# Revit family: xTub_Filler-American_Standard-Fluent-7186_Series
name_source: partatom
category: Plumbing Fixtures
revit_build: Autodesk Revit 2014 (Build: 20130308_1515(x64)
units: mm (PartAtom-declared; Revit-internal decimal feet)

## types (2) — shared parameters
8888.900 Deck-Mount Tub Filler Flex Hose Kit = No
ADA Compliant = Yes
Assembly Code = D2020300
CW Connection = Yes
CWFU = 3
Cold Water Connection Diameter = 3/4"
Default Elevation = 0"
Finish = Metal-American Standard-002-Polished Chrome
Flow Rate = 2.5 GPM (9.5 L/min)
HW Connection = Yes
HWFU = 3
Height = 8 5/8"
Hot Water Connection Diameter = 3/4"
Installation Type = Deck Mounted
Length = 9 3/4"
Manufacturer = American Standard
Material = Metal-American Standard-002-Polished Chrome
Price = Prices may vary. Please consult Manufacturer Representative for most up-to-date price list.
Product Documentation Link = https://www.americanstandard-us.com
Product Page URL = https://www.americanstandard-us.com
Specification = Two-handle deck-mount tub filler shall feature brass construction with brass and copper waterway. Shall also feature 1/4 turn washerless ceramic disc valve cartridges.
URL = http://www.americanstandard-us.com
Vent Connection = No
WFU = 4
Waste Connection = No
Width = 16 1/2"

## per-type parameters (varying)
| type | Description | Inlet Diameter Connection | Personal Shower | Shower Connection Description |
| 7186.901 | Fluent Deck-Mount Tub Filler Personal shower. Metal lever handles. | 1 3/16" | Yes | 1 3/16'' Water Inlet |
| 7186.900 | Fluent Deck-Mount Tub Filler LESS personal shower. Metal lever handles. | 0" | No |  |

note: column(s) folded — value = type name in every type: Model

## geometry (parser evidence)
native form markers: Sweep x2
no freeform markers — native parametric forms only
